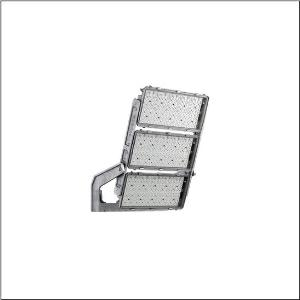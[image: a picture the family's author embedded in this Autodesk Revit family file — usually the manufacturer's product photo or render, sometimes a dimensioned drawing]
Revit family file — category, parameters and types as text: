
# Revit family: floodlight_fl_11_maxi_pro_remote___pl43_5xa779426a01ba_bd65
name_source: partatom
category: Lighting Fixtures
units: mm (PartAtom-declared; Revit-internal decimal feet)

## family parameters
Cut with Voids When Loaded = No
Host = Face
Light Source = No
Part Type = Normal
Room Calculation Point = No
Round Connector Dimension = Use Diameter
Shared = No

## types (1)
- --- (1 x LED, 149370 lm, 1095.8 W, 4000K)
    Apparent Load = 1096 VA
    CIE Flux Codes = 25 74 99 100 100
    Color Rendering = 70
    Color Temperature = 4000K
    Default Elevation = 1800 mm
    Description = Floodlight FL 11  maxi  pro Remote floodlight; light control with lens of PMMA; cover panel of toughened safety glass, transparent; light distribution: PL43, asymmetric direct distribution, LEDcolour temperature: 4000K, rated luminous flux: 149.370lm, colour rendering: CRI > 70, light colour: 740; luminous efficacy: 136lm/W; brightness control: DALI 2 (1 DALI address); with terminal, 8-pole, max. 2.5mm², mains connection: 220..240V/380..400V AC, 50/60Hz, surge voltage resistance: line to ground: 10kV, ECG replaceable separately, no afterglow with DALI off / DMX off command, LED unit replaceable without ESD environment, dustproof LED module, dimming range 10..100%; 1096W floodlight with 2x LED unit of diecast aluminium, coated grey; length: 713mm / width: 651mm / height: 338mm; mounting bracket, of diecast aluminium, uncoated, natural, equipment: Power, protection rating (complete): IP66; insulation class (complete): insulation class I (protective earthing); certification: CE, ENEC, VDE; ball protection: ball impact resistance with accessories, impact resistance: IK07; only for outdoor installations, rated ambient temperature 10°C, permissible operating ambient temperature: -40..+30°C, permissible storage temperature: -40..+85°C; packaging unit: 1 piece

Light Distribution: PL43
    Height = 320 mm
    Lamp = 1 x LED
    Lamp Light Flux = 149370 lm
    Lamp Power = 1095.8 W
    Lamp count = 1
    Length = 1002 mm
    Luminous efficacy = 136 lm/W
    Manufacturer = Siteco
    ModVariant = No
    Model = 5XA779426A01BA
    Mounting Place = Ceiling
    Mounting Type = Surface mounted
    Number of Poles = 1
    OnlyDefault = Yes
    Power Factor = 1
    Product Name = Floodlight FL 11 maxi pro Remote | PL43
    Product group = floodlight | ceiling mounted
    ProductGroupID = 302
    Protection Class = Protection class I
    Protection Degree = IP 66
    RLX_Detail_Level = 1
    RLX_Emergency_Light_Flux = 0 lm
    RLX_Emergency_Type = 0
    RLX_Emergency_Type_DB = No
    RlxData = <blob elided: 52545 chars, md5=22b19a59>
    Socket = socket
    Standby Power = 0 W
    System Light Flux = 149370 lm
    System Power = 1096 W
    Type Comments = factory setting: luminous flux: 100 % | dim-lin: 254 | 760 mA
    Type Image = l_1006784.jpg
    URL = http://relux.com
    VarID = @adj_026805
    Voltage = 0 V
    Weight = 0.00 kg
    Width = 655 mm

## geometry (parser evidence)
native form markers: Blend x4, Sweep x13
no freeform markers — native parametric forms only
